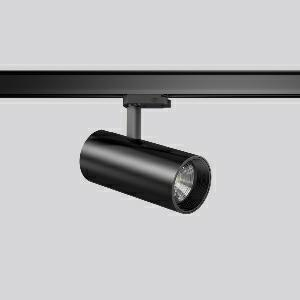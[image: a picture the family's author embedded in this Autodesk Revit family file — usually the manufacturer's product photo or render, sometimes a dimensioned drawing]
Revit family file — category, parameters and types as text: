
# Revit family: deecos_s_mini_742199_003_3_76_f2e6
name_source: partatom
category: Lighting Fixtures
units: mm (PartAtom-declared; Revit-internal decimal feet)

## family parameters
Cut with Voids When Loaded = No
Host = Face
Light Source = No
Part Type = Normal
Room Calculation Point = No
Round Connector Dimension = Use Diameter
Shared = No

## types (1)
- DEECOS S mini (1 x LED Modul 935, 2150 lm, 3500)
    Apparent Load = 20 VA
    Approval mark = CE
    CIE Flux Codes = 96 100 100 100 100
    Color Rendering = 92
    Color Temperature = 3500
    Default Elevation = 1800 mm
    Description = Series: DEECOS S mini
LED surface-mounted projector in modern design with no visible cooling ribs. Housing: die-cast aluminium, powder-coated. Rotation range: 356°. Swivel range: 90°. Black plastic ring and recessed LED to prevent glare from the side. Optical assembly with lens made of plastic (polycarbonate) for the best homogeneous light distribution - can be changed without tools. Best colour rendering index Ra>90. With adapter for RZB 3-circuit DALI tracks. Suitable for Track on ceiling, Wall track. High quality converter without flickering and stroboscopic effect. The following accessories can be mounted without use of tools: interchangeable lenses, decorative glasses, honeycomb louvre, clear and frosted diffusers, white interchangeable plastic ring. 
Colour: deep black, matt (RAL 9005)
Diameter: 87 mm
Height: 214 mm
Lamp: LED
Socket: without socket
Colour temperature: 3500K
Colour rendering index (CRI): 92
System power: 20 W
Rated luminous flux: 2150 lm
Luminous efficiency: 108 lm/W
Control gear: Converter, dimmable, DALI
Protection class: I
Type of protection: IP 20
    Height = 214 mm
    Lamp = 1 x LED Modul 935
    Lamp Light Flux = 2150 lm
    Lamp count = 1
    Length = 87 mm
    Lifetime = 50000 h
    Luminous efficacy = 108 lm/W
    Manufacturer = RZB
    ModVariant = No
    Model = 742199.003.3.76
    Mounting Place = Ceiling
    Mounting Type = Rail mounted
    Number of Poles = 1
    OnlyDefault = Yes
    Power Factor = 1
    Product Name = DEECOS S mini
    Product group = Track mounted projectors
    ProductGroupID = 301
    Protection Class = Protection class I
    Protection Degree = IP 20
    RLX_Detail_Level = 1
    RLX_Emergency_Light_Flux = 0 lm
    RLX_Emergency_Type = 0
    RLX_Emergency_Type_DB = No
    RlxData = <blob elided: 38981 chars, md5=9ff16ad4>
    Socket = socket
    Standby Power = 0 W
    System Light Flux = 2150 lm
    System Power = 20 W
    Type Comments = Product without accessories
    Type Image = 741930.003.jpg
    URL = http://relux.com
    VarID = ---
    Voltage = 230 V
    Voltage Range = 220-240 V
    Weight = 0.00 kg
    Width = 0 mm  [stored 0 ft]

note: [stored X ft] marks values corroborated as IEEE doubles in the binary element streams (Revit-internal decimal feet)

## geometry (parser evidence)
native form markers: Blend x4, Sweep x12
no freeform markers — native parametric forms only
